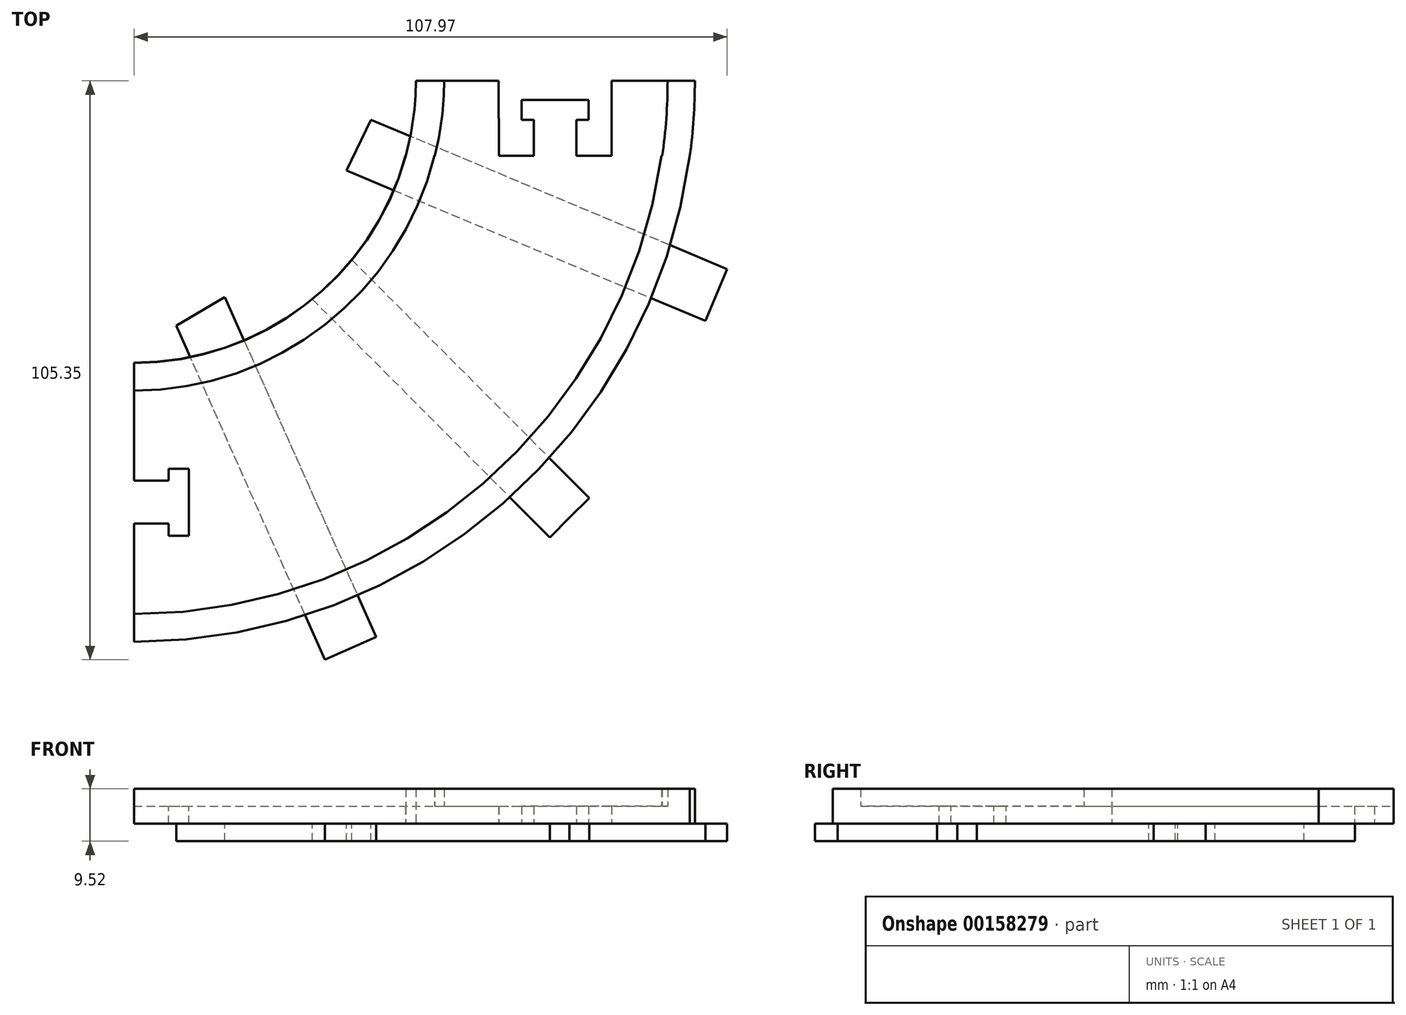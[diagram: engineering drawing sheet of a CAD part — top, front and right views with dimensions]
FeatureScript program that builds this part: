
annotation { "Feature Type Name" : "Feature", "Feature Type Description" : "" }
export const myFeature = defineFeature(function(context is Context, id is Id, definition is map)
    precondition{}
    {
        {
            var Q0;
            Q0=qCreatedBy(makeId("Top.planeOp"),FACE);
            var sketch = newSketch(context, id + "F0", { "sketchPlane" : qUnion([Q0])});
            skCircle(sketch, "E0", {"center": v(0, 0) * mm, "radius": 102.1 * mm});
            skCircle(sketch, "E1", {"center": v(0, 0) * mm, "radius": 51.3 * mm});
            skLineSegment(sketch, "E2", {"start": v(102.1, 0) * mm, "end": v(51.24, 0) * mm});
            skLineSegment(sketch, "E3", {"start": v(0, -51.3) * mm, "end": v(0, -102.1) * mm});
            skLineSegment(sketch, "E4", {"start": v(0, -102.1) * mm, "end": v(-44.33, -102.1) * mm});
            skLineSegment(sketch, "E5", {"start": v(-44.33, -102.1) * mm, "end": v(-44.33, -51.3) * mm});
            skLineSegment(sketch, "E6", {"start": v(-44.33, -51.3) * mm, "end": v(0, -51.3) * mm});
            skLineSegment(sketch, "E7", {"start": v(-16.74, -51.3) * mm, "end": v(-16.74, -102.1) * mm});
            skSolve(sketch);
        }
        {
            var Q0;
            {var subQ3=sQuery(id+"F0.wireOp",EDGE,"E3");Q0=makeQuery(id+"F0.imprint","IMPRINT",FACE,{"disambiguationData":[TD([[makeQuery(id+"F0.imprint","IMPRINT",EDGE,{"derivedFrom":subQ3}),1.0]])]});}
            extrude(context, id + "F1", {"entities" : qUnion([Q0]), "depth" : 3.17 * mm});
        }
        {
            var Q0;
            Q0=qCreatedBy(makeId("Top.planeOp"),FACE);
            var sketch = newSketch(context, id + "F2", { "sketchPlane" : qUnion([Q0])});
            skLineSegment(sketch, "E8", {"start": v(72.75, -7.12) * mm, "end": v(70.54, -7.12) * mm});
            skLineSegment(sketch, "E9", {"start": v(70.54, -7.12) * mm, "end": v(70.54, -3.5) * mm});
            skLineSegment(sketch, "E10", {"start": v(70.54, -3.5) * mm, "end": v(82.76, -3.5) * mm});
            skLineSegment(sketch, "E11", {"start": v(82.76, -3.5) * mm, "end": v(82.76, -7.12) * mm});
            skLineSegment(sketch, "E12", {"start": v(82.76, -7.12) * mm, "end": v(80.55, -7.12) * mm});
            skLineSegment(sketch, "E13", {"start": v(86.95, -13.65) * mm, "end": v(86.95, 0) * mm});
            skLineSegment(sketch, "E14", {"start": v(76.66, 0) * mm, "end": v(86.95, 0) * mm});
            skLineSegment(sketch, "E15", {"start": v(66.37, 0) * mm, "end": v(76.66, 0) * mm});
            skLineSegment(sketch, "E16", {"start": v(66.37, 0) * mm, "end": v(66.44, -13.65) * mm});
            skLineSegment(sketch, "E17", {"start": v(66.44, -13.65) * mm, "end": v(86.95, -13.65) * mm});
            skLineSegment(sketch, "E18", {"start": v(80.55, -7.12) * mm, "end": v(80.55, -13.65) * mm});
            skLineSegment(sketch, "E19", {"start": v(72.75, -7.12) * mm, "end": v(72.75, -13.65) * mm});
            skLineSegment(sketch, "E20", {"start": v(66.44, -13.65) * mm, "end": v(51.75, -13.65) * mm});
            skLineSegment(sketch, "E21", {"start": v(51.75, -13.65) * mm, "end": v(51.75, 0) * mm});
            skLineSegment(sketch, "E22", {"start": v(51.75, 0) * mm, "end": v(66.37, 0) * mm});
            skLineSegment(sketch, "E23", {"start": v(101.03, 0) * mm, "end": v(101.03, 0) * mm});
            skLineSegment(sketch, "E24", {"start": v(101.03, 0) * mm, "end": v(86.95, 0) * mm});
            skLineSegment(sketch, "E25", {"start": v(101.03, 0) * mm, "end": v(101.03, -13.65) * mm});
            skLineSegment(sketch, "E26", {"start": v(101.03, -13.65) * mm, "end": v(86.95, -13.65) * mm});
            skLineSegment(sketch, "E27", {"start": v(51.75, -13.65) * mm, "end": v(47.58, -13.65) * mm});
            skLineSegment(sketch, "E28", {"start": v(47.58, -13.65) * mm, "end": v(47.58, 0) * mm});
            skLineSegment(sketch, "E29", {"start": v(47.58, 0) * mm, "end": v(51.75, 0) * mm});
            skSolve(sketch);
        }
        {
            var Q0;
            Q0=makeQuery(id+"F2.imprint","IMPRINT",FACE,{"disambiguationData":[TD([[makeQuery(id+"F2.imprint","IMPRINT",EDGE,{"derivedFrom":sQuery(id+"F2.wireOp",EDGE,"E8")}),-1.0]])]});
            var Q1;
            Q1=makeQuery(id+"F2.imprint","IMPRINT",FACE,{"disambiguationData":[TD([[makeQuery(id+"F2.imprint","IMPRINT",EDGE,{"derivedFrom":sQuery(id+"F2.wireOp",EDGE,"E16")}),-1.0]])]});
            var Q2;
            Q2=makeQuery(id+"F2.imprint","IMPRINT",FACE,{"disambiguationData":[TD([[makeQuery(id+"F2.imprint","IMPRINT",EDGE,{"derivedFrom":sQuery(id+"F2.wireOp",EDGE,"E13")}),-1.0]])]});
            extrude(context, id + "F3", {"entities" : qUnion([Q0, Q1, Q2]), "operationType" : NewBodyOperationType.ADD, "depth" : 3.17 * mm});
        }
        {
            var Q0;
            Q0=makeQuery(id+"F3.boolean.opBoolean","MERGE",FACE,{"derivedFrom":[makeQuery(id+"F1.opExtrude","CAP_FACE",FACE,{"disambiguationData":[OSD([sQuery(id+"F0.wireOp",EDGE,"E0"),sQuery(id+"F0.wireOp",EDGE,"E1"),sQuery(id+"F0.wireOp",EDGE,"E2"),sQuery(id+"F0.wireOp",EDGE,"E3")])],"isStart":false}),makeQuery(id+"F3.opExtrude","CAP_FACE",FACE,{"disambiguationData":[OSD([sQuery(id+"F2.wireOp",EDGE,"E8"),sQuery(id+"F2.wireOp",EDGE,"E9"),sQuery(id+"F2.wireOp",EDGE,"E10"),sQuery(id+"F2.wireOp",EDGE,"E11"),sQuery(id+"F2.wireOp",EDGE,"E12"),sQuery(id+"F2.wireOp",EDGE,"E17"),sQuery(id+"F2.wireOp",EDGE,"E18"),sQuery(id+"F2.wireOp",EDGE,"E19")])],"isStart":false}),makeQuery(id+"F3.opExtrude","CAP_FACE",FACE,{"disambiguationData":[OSD([sQuery(id+"F2.wireOp",EDGE,"E13"),sQuery(id+"F2.wireOp",EDGE,"HhnOl6Ur-7oBW-enPF-9H80-fVUDD1N4fKMp"),sQuery(id+"F2.wireOp",EDGE,"E23"),sQuery(id+"F2.wireOp",EDGE,"E24")])],"isStart":false}),makeQuery(id+"F3.opExtrude","CAP_FACE",FACE,{"disambiguationData":[OSD([sQuery(id+"F2.wireOp",EDGE,"E16"),sQuery(id+"F2.wireOp",EDGE,"E20"),sQuery(id+"F2.wireOp",EDGE,"E21"),sQuery(id+"F2.wireOp",EDGE,"E22")])],"isStart":false})]});
            var sketch = newSketch(context, id + "F4", { "sketchPlane" : qUnion([Q0])});
            skCircle(sketch, "E30", {"center": v(0, 0) * mm, "radius": 56.38 * mm});
            skCircle(sketch, "E31", {"center": v(0, 0) * mm, "radius": 97.01 * mm});
            skCircle(sketch, "E32", {"center": v(0, 0) * mm, "radius": 51.33 * mm});
            skCircle(sketch, "E33", {"center": v(0, 0) * mm, "radius": 102.28 * mm});
            skLineSegment(sketch, "E34", {"start": v(0, 0) * mm, "end": v(0, -102.1) * mm});
            skLineSegment(sketch, "E35", {"start": v(0, 0) * mm, "end": v(102.1, 0) * mm});
            skSolve(sketch);
        }
        {
            var Q0;
            {var subQ0=sQuery(id+"F4.wireOp",EDGE,"E35");var subQ1=sQuery(id+"F4.wireOp",EDGE,"E30");var subQ2=makeQuery(id+"F4.imprint","INTERSECT",VERTEX,{"derivedFrom":[subQ1,subQ0]});Q0=makeQuery(id+"F4.imprint","IMPRINT",FACE,{"disambiguationData":[TD([[makeQuery(id+"F4.imprint","IMPRINT",EDGE,{"disambiguationData":[TD([[subQ2,1.0]])],"derivedFrom":subQ1}),1.0]])]});}
            var Q1;
            {var subQ4=makeQuery(id+"F1.opExtrude","CAP_EDGE",EDGE,{"disambiguationData":[OSD([sQuery(id+"F0.wireOp",EDGE,"E0")])],"isStart":false});Q1=makeQuery(id+"F4.imprint","IMPRINT",FACE,{"disambiguationData":[TD([[makeQuery(id+"F4.imprint","IMPRINT",EDGE,{"derivedFrom":subQ4}),1.0]])]});}
            extrude(context, id + "F5", {"entities" : qUnion([Q0, Q1]), "operationType" : NewBodyOperationType.ADD, "depth" : 3.17 * mm});
        }
        {
            var Q0;
            Q0=makeQuery(id+"F2.imprint","IMPRINT",FACE,{"disambiguationData":[TD([[makeQuery(id+"F2.imprint","IMPRINT",EDGE,{"derivedFrom":sQuery(id+"F2.wireOp",EDGE,"E16")}),-1.0]])]});
            var Q1;
            Q1=makeQuery(id+"F2.imprint","IMPRINT",FACE,{"disambiguationData":[TD([[makeQuery(id+"F2.imprint","IMPRINT",EDGE,{"derivedFrom":sQuery(id+"F2.wireOp",EDGE,"E8")}),1.0]])]});
            var Q2;
            Q2=makeQuery(id+"F2.imprint","IMPRINT",FACE,{"disambiguationData":[TD([[makeQuery(id+"F2.imprint","IMPRINT",EDGE,{"derivedFrom":sQuery(id+"F2.wireOp",EDGE,"E13")}),-1.0]])]});
            var Q3;
            Q3=makeQuery(id+"F2.imprint","IMPRINT",FACE,{"disambiguationData":[TD([[makeQuery(id+"F2.imprint","IMPRINT",EDGE,{"derivedFrom":sQuery(id+"F2.wireOp",EDGE,"E21")}),1.0]])]});
            extrude(context, id + "F6", {"entities" : qUnion([Q0, Q1, Q2, Q3]), "operationType" : NewBodyOperationType.REMOVE, "depth" : 25.4 * mm});
        }
        {
            var Q0;
            Q0=qCreatedBy(makeId("Top.planeOp"),FACE);
            var sketch = newSketch(context, id + "F7", { "sketchPlane" : qUnion([Q0])});
            skCircle(sketch, "E36", {"center": v(0, 0) * mm, "radius": 56.44 * mm});
            skCircle(sketch, "E37", {"center": v(0, 0) * mm, "radius": 51.3 * mm});
            skCircle(sketch, "E38", {"center": v(0, 0) * mm, "radius": 102.1 * mm});
            skCircle(sketch, "E39", {"center": v(0, 0) * mm, "radius": 97.14 * mm});
            skLineSegment(sketch, "E40", {"start": v(0, 0) * mm, "end": v(102.1, 0) * mm});
            skLineSegment(sketch, "E41", {"start": v(0, 0) * mm, "end": v(0, -102.1) * mm});
            skLineSegment(sketch, "E42", {"start": v(49.45, -13.66) * mm, "end": v(101.19, -13.66) * mm});
            skSolve(sketch);
        }
        {
            var Q0;
            {var subQ0=sQuery(id+"F7.wireOp",EDGE,"E40");var subQ1=sQuery(id+"F7.wireOp",EDGE,"E36");var subQ2=makeQuery(id+"F7.imprint","INTERSECT",VERTEX,{"derivedFrom":[subQ1,subQ0]});Q0=makeQuery(id+"F7.imprint","IMPRINT",FACE,{"disambiguationData":[TD([[makeQuery(id+"F7.imprint","IMPRINT",EDGE,{"disambiguationData":[TD([[subQ2,1.0]])],"derivedFrom":subQ1}),1.0]])]});}
            var Q1;
            {var subQ0=sQuery(id+"F7.wireOp",EDGE,"E40");var subQ1=sQuery(id+"F7.wireOp",EDGE,"E38");var subQ2=makeQuery(id+"F7.imprint","INTERSECT",VERTEX,{"derivedFrom":[subQ1,subQ0]});Q1=makeQuery(id+"F7.imprint","IMPRINT",FACE,{"disambiguationData":[TD([[makeQuery(id+"F7.imprint","IMPRINT",EDGE,{"disambiguationData":[TD([[subQ2,1.0]])],"derivedFrom":subQ1}),1.0]])]});}
            extrude(context, id + "F8", {"entities" : qUnion([Q0, Q1]), "operationType" : NewBodyOperationType.ADD, "depth" : 6.35 * mm});
        }
        {
            var Q0;
            Q0=makeQuery(id+"F2.imprint","IMPRINT",FACE,{"disambiguationData":[TD([[makeQuery(id+"F2.imprint","IMPRINT",EDGE,{"derivedFrom":sQuery(id+"F2.wireOp",EDGE,"E13")}),-1.0]])]});
            var Q1;
            Q1=makeQuery(id+"F2.imprint","IMPRINT",FACE,{"disambiguationData":[TD([[makeQuery(id+"F2.imprint","IMPRINT",EDGE,{"derivedFrom":sQuery(id+"F2.wireOp",EDGE,"E16")}),-1.0]])]});
            extrude(context, id + "F9", {"entities" : qUnion([Q0, Q1]), "operationType" : NewBodyOperationType.ADD, "depth" : 3.17 * mm});
        }
        {
            var Q0;
            {var subQ1=sQuery(id+"F4.wireOp",EDGE,"E30");var subQ2=sQuery(id+"F0.wireOp",EDGE,"E3");var subQ5=sQuery(id+"F0.wireOp",EDGE,"E2");var subQ7=sQuery(id+"F0.wireOp",EDGE,"E0");Q0=makeQuery(id+"F9.boolean.opBoolean","MERGE",FACE,{"derivedFrom":[makeQuery(id+"F5.boolean.opBoolean","SPLIT",FACE,{"disambiguationData":[TD([makeQuery(id+"F5.opExtrude","SWEPT_FACE",FACE,{"disambiguationData":[OSD([subQ1])]})])],"derivedFrom":makeQuery(id+"F1.opExtrude","CAP_FACE",FACE,{"disambiguationData":[OSD([subQ7,sQuery(id+"F0.wireOp",EDGE,"E1"),subQ5,subQ2])],"isStart":false})}),makeQuery(id+"F9.opExtrude","CAP_FACE",FACE,{"disambiguationData":[OSD([sQuery(id+"F2.wireOp",EDGE,"E13"),sQuery(id+"F2.wireOp",EDGE,"E24"),sQuery(id+"F2.wireOp",EDGE,"E25"),sQuery(id+"F2.wireOp",EDGE,"E26")])],"isStart":false}),makeQuery(id+"F9.opExtrude","CAP_FACE",FACE,{"disambiguationData":[OSD([sQuery(id+"F2.wireOp",EDGE,"E16"),sQuery(id+"F2.wireOp",EDGE,"E20"),sQuery(id+"F2.wireOp",EDGE,"E21"),sQuery(id+"F2.wireOp",EDGE,"E22")])],"isStart":false})]});}
            var sketch = newSketch(context, id + "F10", { "sketchPlane" : qUnion([Q0])});
            skLineSegment(sketch, "E43.top", {"start": v(-0.16, -51.2) * mm, "end": v(-0.16, -102) * mm});
            skLineSegment(sketch, "E44", {"start": v(-0.16, -66.3) * mm, "end": v(-0.16, -72.78) * mm});
            skLineSegment(sketch, "E45", {"start": v(-0.16, -72.78) * mm, "end": v(6.31, -72.78) * mm});
            skLineSegment(sketch, "E46", {"start": v(6.31, -72.78) * mm, "end": v(6.31, -70.57) * mm});
            skLineSegment(sketch, "E47", {"start": v(6.31, -70.57) * mm, "end": v(10, -70.57) * mm});
            skLineSegment(sketch, "E48", {"start": v(10, -70.57) * mm, "end": v(10, -82.78) * mm});
            skLineSegment(sketch, "E49", {"start": v(10, -82.78) * mm, "end": v(6.31, -82.78) * mm});
            skLineSegment(sketch, "E50", {"start": v(6.31, -82.78) * mm, "end": v(6.31, -80.57) * mm});
            skLineSegment(sketch, "E51", {"start": v(6.31, -80.57) * mm, "end": v(-0.16, -80.57) * mm});
            skLineSegment(sketch, "E52", {"start": v(-0.16, -80.57) * mm, "end": v(-0.16, -87.04) * mm});
            skLineSegment(sketch, "E53", {"start": v(-0.16, -87.04) * mm, "end": v(13.49, -87.04) * mm});
            skLineSegment(sketch, "E54", {"start": v(13.49, -76.75) * mm, "end": v(13.49, -87.04) * mm});
            skLineSegment(sketch, "E55", {"start": v(13.49, -66.46) * mm, "end": v(13.49, -76.75) * mm});
            skLineSegment(sketch, "E56", {"start": v(13.49, -66.46) * mm, "end": v(-0.16, -66.46) * mm});
            skLineSegment(sketch, "E57", {"start": v(-0.16, -66.46) * mm, "end": v(-0.16, -87.04) * mm});
            skLineSegment(sketch, "E58", {"start": v(13.49, -66.46) * mm, "end": v(13.49, -51.2) * mm});
            skLineSegment(sketch, "E59", {"start": v(13.49, -51.2) * mm, "end": v(13.49, -87.04) * mm});
            skLineSegment(sketch, "E60", {"start": v(13.49, -87.04) * mm, "end": v(13.49, -102) * mm});
            skLineSegment(sketch, "E61", {"start": v(13.49, -51.2) * mm, "end": v(-0.16, -51.2) * mm});
            skLineSegment(sketch, "E62", {"start": v(13.49, -102) * mm, "end": v(-0.16, -102) * mm});
            skSolve(sketch);
        }
        {
            var Q0;
            {var subQ10=sQuery(id+"F10.wireOp",EDGE,"E46");Q0=makeQuery(id+"F10.imprint","IMPRINT",FACE,{"disambiguationData":[TD([[makeQuery(id+"F10.imprint","IMPRINT",EDGE,{"derivedFrom":subQ10}),-1.0]])]});}
            extrude(context, id + "F11", {"entities" : qUnion([Q0]), "operationType" : NewBodyOperationType.REMOVE, "oppositeDirection" : true, "depth" : 25.4 * mm});
        }
        {
            var Q0;
            {var subQ0=sQuery(id+"F7.wireOp",EDGE,"E42");var subQ1=sQuery(id+"F7.wireOp",EDGE,"E40");Q0=makeQuery(id+"F9.boolean.opBoolean","MERGE",FACE,{"derivedFrom":[makeQuery(id+"F8.boolean.opBoolean","MERGE",FACE,{"derivedFrom":[makeQuery(id+"F1.opExtrude","CAP_FACE",FACE,{"disambiguationData":[OSD([sQuery(id+"F0.wireOp",EDGE,"E0"),sQuery(id+"F0.wireOp",EDGE,"E1"),sQuery(id+"F0.wireOp",EDGE,"E2"),sQuery(id+"F0.wireOp",EDGE,"E3")])],"isStart":true}),makeQuery(id+"F8.opExtrude","CAP_FACE",FACE,{"disambiguationData":[OSD([sQuery(id+"F7.wireOp",EDGE,"E36"),sQuery(id+"F7.wireOp",EDGE,"E37"),subQ1,subQ0])],"isStart":true}),makeQuery(id+"F8.opExtrude","CAP_FACE",FACE,{"disambiguationData":[OSD([sQuery(id+"F7.wireOp",EDGE,"E38"),sQuery(id+"F7.wireOp",EDGE,"E39"),subQ1,subQ0])],"isStart":true})]}),makeQuery(id+"F9.opExtrude","CAP_FACE",FACE,{"disambiguationData":[OSD([sQuery(id+"F2.wireOp",EDGE,"E13"),sQuery(id+"F2.wireOp",EDGE,"E24"),sQuery(id+"F2.wireOp",EDGE,"E25"),sQuery(id+"F2.wireOp",EDGE,"E26")])],"isStart":true}),makeQuery(id+"F9.opExtrude","CAP_FACE",FACE,{"disambiguationData":[OSD([sQuery(id+"F2.wireOp",EDGE,"E16"),sQuery(id+"F2.wireOp",EDGE,"E20"),sQuery(id+"F2.wireOp",EDGE,"E21"),sQuery(id+"F2.wireOp",EDGE,"E22")])],"isStart":true})]});}
            var sketch = newSketch(context, id + "F12", { "sketchPlane" : qUnion([Q0])});
            skLineSegment(sketch, "E63", {"start": v(72.1, 72.28) * mm, "end": v(0, 0) * mm});
            skLineSegment(sketch, "E64", {"start": v(72.1, 72.28) * mm, "end": v(79.27, 79.48) * mm});
            skLineSegment(sketch, "E65", {"start": v(36.22, 36.32) * mm, "end": v(29.05, 29.12) * mm});
            skLineSegment(sketch, "E66", {"start": v(29.05, 29.12) * mm, "end": v(25.45, 32.71) * mm});
            skLineSegment(sketch, "E67", {"start": v(29.05, 29.12) * mm, "end": v(32.65, 25.54) * mm});
            skLineSegment(sketch, "E68", {"start": v(25.45, 32.71) * mm, "end": v(75.73, 83.12) * mm});
            skLineSegment(sketch, "E69", {"start": v(75.73, 83.12) * mm, "end": v(79.27, 79.48) * mm});
            skLineSegment(sketch, "E70", {"start": v(32.65, 25.54) * mm, "end": v(82.88, 75.9) * mm});
            skLineSegment(sketch, "E71", {"start": v(82.88, 75.9) * mm, "end": v(79.27, 79.48) * mm});
            skLineSegment(sketch, "E72", {"start": v(25.45, 32.71) * mm, "end": v(16.52, 39.32) * mm});
            skLineSegment(sketch, "E73", {"start": v(32.65, 25.54) * mm, "end": v(38.71, 16.31) * mm});
            skLineSegment(sketch, "E74", {"start": v(38.71, 16.31) * mm, "end": v(104.01, 43.7) * mm});
            skLineSegment(sketch, "E75", {"start": v(104.01, 43.7) * mm, "end": v(107.97, 34.26) * mm});
            skLineSegment(sketch, "E76", {"start": v(107.97, 34.26) * mm, "end": v(43.16, 7.08) * mm});
            skLineSegment(sketch, "E77", {"start": v(43.16, 7.08) * mm, "end": v(38.71, 16.31) * mm});
            skLineSegment(sketch, "E78", {"start": v(16.52, 39.32) * mm, "end": v(44.06, 101.21) * mm});
            skLineSegment(sketch, "E79", {"start": v(44.06, 101.21) * mm, "end": v(34.76, 105.35) * mm});
            skLineSegment(sketch, "E80", {"start": v(34.76, 105.35) * mm, "end": v(7.71, 44.58) * mm});
            skLineSegment(sketch, "E81", {"start": v(7.71, 44.58) * mm, "end": v(16.52, 39.32) * mm});
            skSolve(sketch);
        }
        {
            var Q0;
            {var subQ0=sQuery(id+"F12.wireOp",EDGE,"E65");Q0=makeQuery(id+"F12.imprint","IMPRINT",FACE,{"disambiguationData":[TD([[makeQuery(id+"F12.imprint","IMPRINT",EDGE,{"derivedFrom":subQ0}),1.0]])]});}
            var Q1;
            {var subQ0=sQuery(id+"F12.wireOp",EDGE,"E65");Q1=makeQuery(id+"F12.imprint","IMPRINT",FACE,{"disambiguationData":[TD([[makeQuery(id+"F12.imprint","IMPRINT",EDGE,{"derivedFrom":subQ0}),-1.0]])]});}
            var Q2;
            {var subQ1=makeQuery(id+"F1.opExtrude","CAP_EDGE",EDGE,{"disambiguationData":[OSD([sQuery(id+"F0.wireOp",EDGE,"E0")])],"isStart":true});var subQ5=sQuery(id+"F12.wireOp",EDGE,"E68");var subQ6=makeQuery(id+"F12.imprint","INTERSECT",VERTEX,{"derivedFrom":[subQ1,subQ5]});Q2=makeQuery(id+"F12.imprint","IMPRINT",FACE,{"disambiguationData":[TD([[makeQuery(id+"F12.imprint","IMPRINT",EDGE,{"disambiguationData":[TD([[subQ6,1.0]])],"derivedFrom":subQ5}),-1.0]])]});}
            var Q3;
            {var subQ1=makeQuery(id+"F1.opExtrude","CAP_EDGE",EDGE,{"disambiguationData":[OSD([sQuery(id+"F0.wireOp",EDGE,"E0")])],"isStart":true});var subQ5=sQuery(id+"F12.wireOp",EDGE,"E70");var subQ6=makeQuery(id+"F12.imprint","INTERSECT",VERTEX,{"derivedFrom":[subQ1,subQ5]});Q3=makeQuery(id+"F12.imprint","IMPRINT",FACE,{"disambiguationData":[TD([[makeQuery(id+"F12.imprint","IMPRINT",EDGE,{"disambiguationData":[TD([[subQ6,1.0]])],"derivedFrom":subQ5}),1.0]])]});}
            var Q4;
            {var subQ0=sQuery(id+"F12.wireOp",EDGE,"E64");Q4=makeQuery(id+"F12.imprint","IMPRINT",FACE,{"disambiguationData":[TD([[makeQuery(id+"F12.imprint","IMPRINT",EDGE,{"derivedFrom":subQ0}),-1.0]])]});}
            var Q5;
            {var subQ0=sQuery(id+"F12.wireOp",EDGE,"E64");Q5=makeQuery(id+"F12.imprint","IMPRINT",FACE,{"disambiguationData":[TD([[makeQuery(id+"F12.imprint","IMPRINT",EDGE,{"derivedFrom":subQ0}),1.0]])]});}
            var Q6;
            {var subQ0=sQuery(id+"F12.wireOp",EDGE,"E78");var subQ1=makeQuery(id+"F1.opExtrude","CAP_EDGE",EDGE,{"disambiguationData":[OSD([sQuery(id+"F0.wireOp",EDGE,"E0")])],"isStart":true});var subQ2=makeQuery(id+"F12.imprint","INTERSECT",VERTEX,{"derivedFrom":[subQ1,subQ0]});Q6=makeQuery(id+"F12.imprint","IMPRINT",FACE,{"disambiguationData":[TD([[makeQuery(id+"F12.imprint","IMPRINT",EDGE,{"disambiguationData":[TD([[subQ2,1.0]])],"derivedFrom":subQ0}),1.0]])]});}
            var Q7;
            {var subQ0=sQuery(id+"F12.wireOp",EDGE,"E79");Q7=makeQuery(id+"F12.imprint","IMPRINT",FACE,{"disambiguationData":[TD([[makeQuery(id+"F12.imprint","IMPRINT",EDGE,{"derivedFrom":subQ0}),1.0]])]});}
            var Q8;
            {var subQ0=sQuery(id+"F12.wireOp",EDGE,"E81");Q8=makeQuery(id+"F12.imprint","IMPRINT",FACE,{"disambiguationData":[TD([[makeQuery(id+"F12.imprint","IMPRINT",EDGE,{"derivedFrom":subQ0}),1.0]])]});}
            var Q9;
            {var subQ8=sQuery(id+"F12.wireOp",EDGE,"E77");Q9=makeQuery(id+"F12.imprint","IMPRINT",FACE,{"disambiguationData":[TD([[makeQuery(id+"F12.imprint","IMPRINT",EDGE,{"derivedFrom":subQ8}),-1.0]])]});}
            var Q10;
            {var subQ7=sQuery(id+"F0.wireOp",EDGE,"E0");var subQ10=sQuery(id+"F12.wireOp",EDGE,"E74");var subQ13=makeQuery(id+"F1.opExtrude","CAP_EDGE",EDGE,{"disambiguationData":[OSD([subQ7])],"isStart":true});var subQ17=makeQuery(id+"F12.imprint","INTERSECT",VERTEX,{"derivedFrom":[subQ13,subQ10]});Q10=makeQuery(id+"F12.imprint","IMPRINT",FACE,{"disambiguationData":[TD([[makeQuery(id+"F12.imprint","IMPRINT",EDGE,{"disambiguationData":[TD([[subQ17,1.0]])],"derivedFrom":subQ10}),-1.0]])]});}
            var Q11;
            {var subQ0=sQuery(id+"F12.wireOp",EDGE,"E75");Q11=makeQuery(id+"F12.imprint","IMPRINT",FACE,{"disambiguationData":[TD([[makeQuery(id+"F12.imprint","IMPRINT",EDGE,{"derivedFrom":subQ0}),-1.0]])]});}
            extrude(context, id + "F13", {"entities" : qUnion([Q0, Q1, Q2, Q3, Q4, Q5, Q6, Q7, Q8, Q9, Q10, Q11]), "operationType" : NewBodyOperationType.ADD, "depth" : 3.17 * mm});
        }
    });
